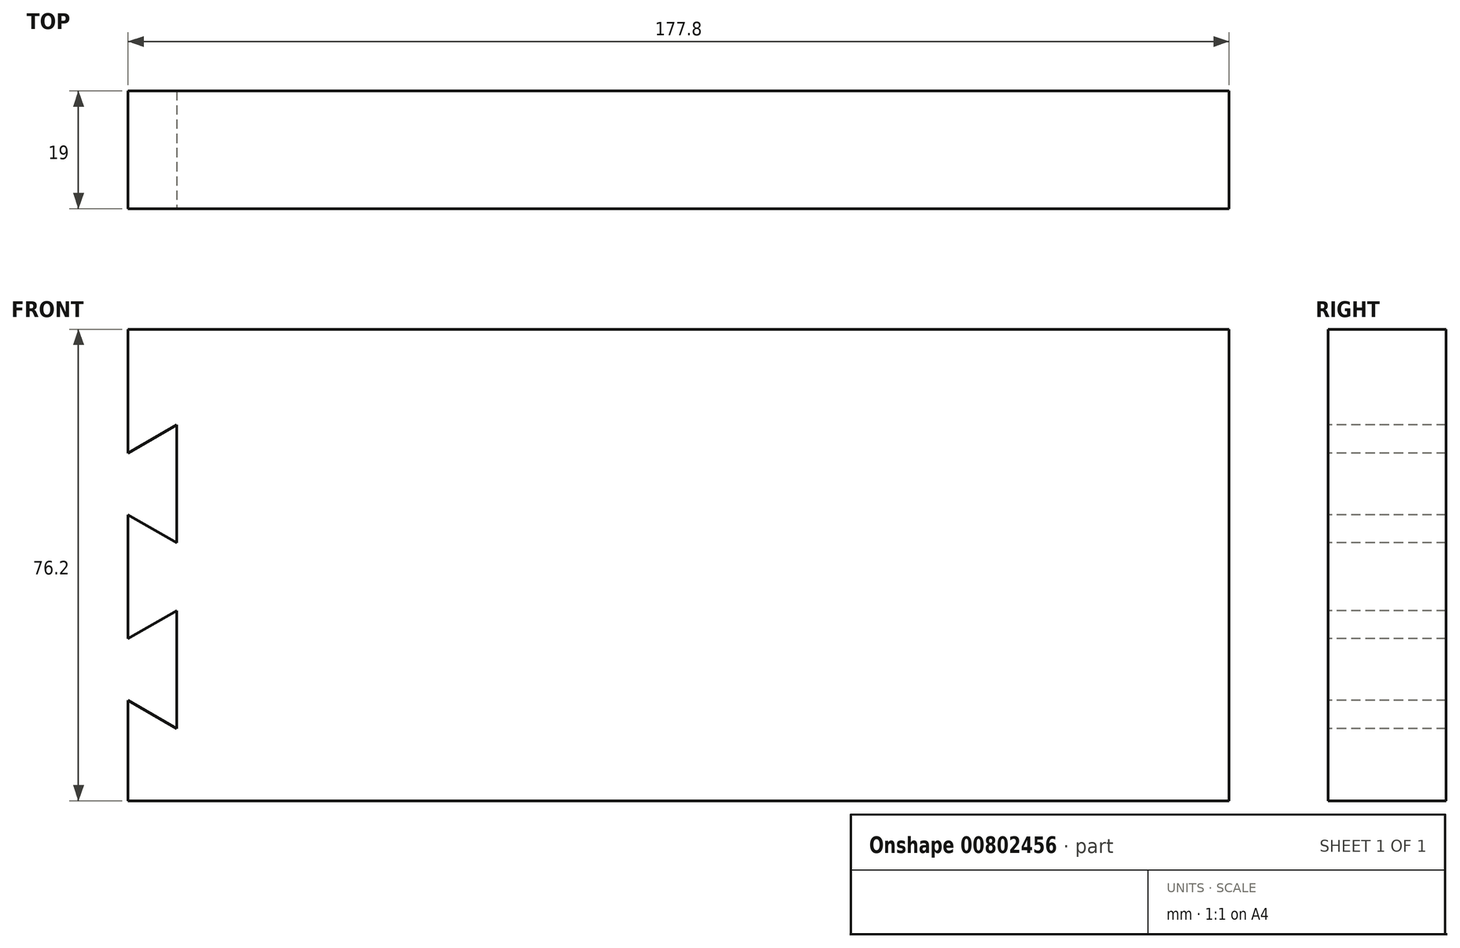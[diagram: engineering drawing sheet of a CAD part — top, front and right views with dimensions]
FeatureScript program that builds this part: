
annotation { "Feature Type Name" : "Feature", "Feature Type Description" : "" }
export const myFeature = defineFeature(function(context is Context, id is Id, definition is map)
    precondition{}
    {
        {
            var Q0;
            Q0=qCreatedBy(makeId("Front.planeOp"),FACE);
            var sketch = newSketch(context, id + "F0", { "sketchPlane" : qUnion([Q0])});
            skLineSegment(sketch, "E0", {"start": v(0, 0) * mm, "end": v(177.8, 0) * mm});
            skLineSegment(sketch, "E1", {"start": v(177.8, 0) * mm, "end": v(177.8, 76.2) * mm});
            skLineSegment(sketch, "E2", {"start": v(177.8, 76.2) * mm, "end": v(0, 76.2) * mm});
            skLineSegment(sketch, "E3", {"start": v(0, 76.2) * mm, "end": v(0, 56.2) * mm});
            skLineSegment(sketch, "E4", {"start": v(0, 56.2) * mm, "end": v(7.84, 60.73) * mm});
            skLineSegment(sketch, "E5", {"start": v(7.84, 60.73) * mm, "end": v(7.84, 41.68) * mm});
            skLineSegment(sketch, "E6", {"start": v(7.84, 41.68) * mm, "end": v(0, 46.2) * mm});
            skLineSegment(sketch, "E7", {"start": v(0, 46.2) * mm, "end": v(0, 26.2) * mm});
            skLineSegment(sketch, "E8", {"start": v(0, 26.2) * mm, "end": v(7.84, 30.73) * mm});
            skLineSegment(sketch, "E9", {"start": v(7.84, 30.73) * mm, "end": v(7.84, 11.68) * mm});
            skLineSegment(sketch, "E10", {"start": v(7.84, 11.68) * mm, "end": v(0, 16.2) * mm});
            skLineSegment(sketch, "E11", {"start": v(0, 16.2) * mm, "end": v(0, 0) * mm});
            skSolve(sketch);
        }
        {
            var Q0;
            Q0=makeQuery(id+"F0.imprint","IMPRINT",FACE,{"disambiguationData":[TD([[makeQuery(id+"F0.imprint","IMPRINT",EDGE,{"derivedFrom":sQuery(id+"F0.wireOp",EDGE,"E0")}),1.0]])]});
            extrude(context, id + "F1", {"entities" : qUnion([Q0]), "oppositeDirection" : true, "depth" : 19 * mm, "offsetDistance" : 25 * mm});
        }
    });
